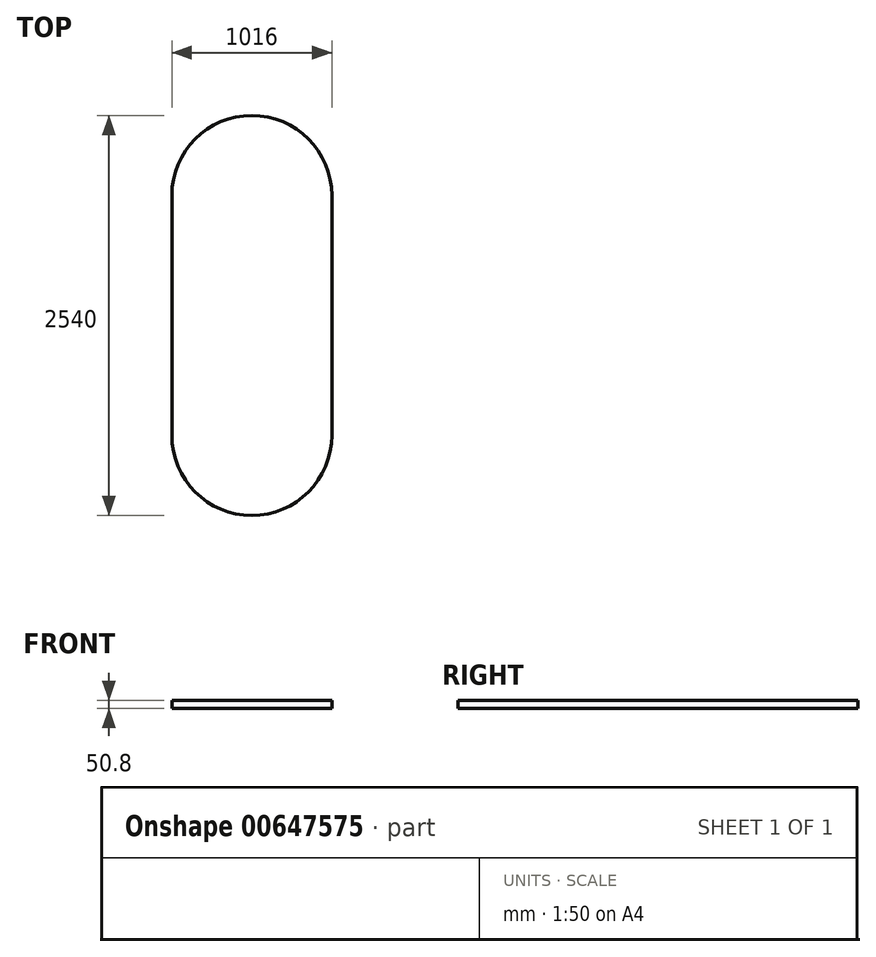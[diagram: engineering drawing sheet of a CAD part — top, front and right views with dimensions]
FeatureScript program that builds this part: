
annotation { "Feature Type Name" : "Feature", "Feature Type Description" : "" }
export const myFeature = defineFeature(function(context is Context, id is Id, definition is map)
    precondition{}
    {
        {
            var Q0;
            Q0=qCreatedBy(makeId("Top.planeOp"),FACE);
            var sketch = newSketch(context, id + "F0", { "sketchPlane" : qUnion([Q0])});
            skLineSegment(sketch, "E0.left", {"start": v(-508, 762) * mm, "end": v(-508, -762) * mm});
            skLineSegment(sketch, "E0.right", {"start": v(508, 762) * mm, "end": v(508, -762) * mm});
            skArc(sketch, "E1", {"start": v(-508, 762) * mm, "mid": v(0, 1270) * mm, "end": v(508, 762) * mm});
            skArc(sketch, "E2", {"start": v(-508, -762) * mm, "mid": v(0, -1270) * mm, "end": v(508, -762) * mm});
            skSolve(sketch);
        }
        {
            var Q0;
            Q0=makeQuery(id+"F0.imprint","IMPRINT",FACE,{"disambiguationData":[TD([[makeQuery(id+"F0.imprint","IMPRINT",EDGE,{"derivedFrom":sQuery(id+"F0.wireOp",EDGE,"E0.left")}),1.0]])]});
            extrude(context, id + "F1", {"entities" : qUnion([Q0]), "depth" : 50.8 * mm, "offsetDistance" : 25 * mm});
        }
    });
